# Revit family: Micropoint 2 Recessed
name_source: partatom
category: Lighting Fixtures
revit_build: Autodesk Revit MEP 2012 (Build: 20110916_2132(x64)
units: mm (PartAtom-declared; Revit-internal decimal feet)

## types (2) — shared parameters
Apparent Load = 2 VA
Body Material = Eaton – (Body, Polycarbonate, RAL9016)
Circuit Watts = 2 W
Color Filter = 16777215
Cutout Diameter = 64 mm  [stored 0.209974 ft]
Diameter = 90 mm  [stored 0.295276 ft]
Dimming Lamp Color Temperature Shift = <None>
Emergency = Yes
Height = 63 mm  [stored 0.206693 ft]
IP Rating = IP44
LOR = 1
Lamp = LED
Lamp Material = Eaton – (Lamp, Glass, Self Illuminating)
Manufacturer = EATON
Model = MICROPOINT 2
Power Factor = 0.7
Special Considerations 1 = Maintained luminaire can be operated in non maintained mode
Special Considerations 2 = Can be supplied to operate with CBU/CEAG System
Tilt Angle = -90.00°
URL = http://www.cooper-ls.com
Voltage = 230 V
Wattage Comments = LED
Weight = 0.45
zero-valued in all types: Default Elevation

## per-type parameters (varying)
| type | Description | E | Photometric Web File |
| MP2E3H | Micropoint 2 Flush mounted self contained/slave 2W LED Escape Route emergency luminaire. retained in ceiling with spring fixing requiring front access only. Battery and control gear mounted in remote pod with plug in connections | Yes | MP2E3H.IES |
| MP2O3H | Micropoint 2 Flush mounted self contained/slave 2W LED open area emergency luminaire. retained in ceiling with spring fixing requiring front access only. Battery and control gear mounted in remote pod with plug in connections | No | MP2O3H.IES |

note: column(s) folded — value = type name in every type: Part No.

note: [stored X ft] marks values corroborated as IEEE doubles in the binary element streams (Revit-internal decimal feet)

## geometry (parser evidence)
native form markers: Blend x1, Sweep x1
no freeform markers — native parametric forms only
